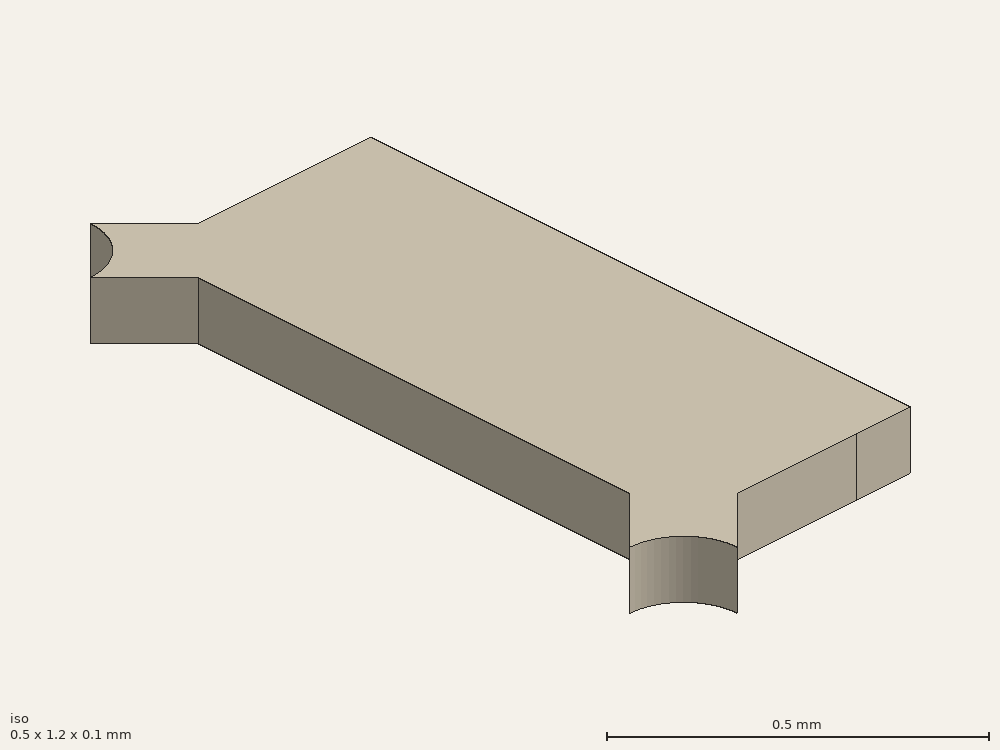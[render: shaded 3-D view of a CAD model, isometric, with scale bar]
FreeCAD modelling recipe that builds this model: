
FCSTD DOCUMENT  (FreeCAD 0.17R12607 (Git))
Label: FC-12M PAD 2bis
License: CreativeCommons Attribution-ShareAlike
LicenseURL: http://creativecommons.org/licenses/by-sa/4.0/
objects: Sketcher::SketchObject×1, PartDesign::Pad×1, PartDesign::Body×1
note: 4 computed .brp shape members not serialized (recipe doc carries the construction recipe); baked Part::Feature solids carry a one-line shape summary decoded from their .brp

FEATURE [Sketcher::SketchObject] Sketch
  MapMode = 5
  Support = -> [XY_Plane]
  sketch-geometry (19):
    g0: LineSegment StartX=-0.5 StartY=0.4 StartZ=0 EndX=-0.5 EndY=-0.4 EndZ=0
    g1: LineSegment [constr] StartX=-0.5 StartY=-0.4 StartZ=0 EndX=-0.6 EndY=-0.5 EndZ=0
    g2: LineSegment StartX=-0.6 StartY=-0.5 StartZ=0 EndX=-0.82 EndY=-0.5 EndZ=0
    g3: LineSegment StartX=-0.82 StartY=-0.5 StartZ=0 EndX=-0.92 EndY=-0.6 EndZ=0
    g4: LineSegment [constr] StartX=-0.92 StartY=-0.6 StartZ=0 EndX=-1.02 EndY=-0.5 EndZ=0
    g5: LineSegment StartX=-1.02 StartY=-0.5 StartZ=0 EndX=-0.92 EndY=-0.4 EndZ=0
    g6: LineSegment StartX=-0.92 StartY=-0.4 StartZ=0 EndX=-0.92 EndY=0.4 EndZ=0
    g7: LineSegment StartX=-0.92 StartY=0.4 StartZ=0 EndX=-1.02 EndY=0.5 EndZ=0
    g8: LineSegment [constr] StartX=-1.02 StartY=0.5 StartZ=0 EndX=-0.92 EndY=0.6 EndZ=0
    g9: LineSegment StartX=-0.92 StartY=0.6 StartZ=0 EndX=-0.82 EndY=0.5 EndZ=0
    g10: LineSegment StartX=-0.82 StartY=0.5 StartZ=0 EndX=-0.6 EndY=0.5 EndZ=0
    g11: LineSegment [constr] StartX=-0.6 StartY=0.5 StartZ=0 EndX=-0.5 EndY=0.4 EndZ=0
    g12: ArcOfCircle CenterX=-1.02 CenterY=0.6 CenterZ=0 NormalX=0 NormalY=0 NormalZ=1 AngleXU=0 Radius=0.1 StartAngle=4.71239 EndAngle=6.28319
    g13: LineSegment [constr] StartX=-1.02 StartY=0.5 StartZ=0 EndX=-0.82 EndY=0.5 EndZ=0
    g14: ArcOfCircle CenterX=-1.02 CenterY=-0.6 CenterZ=0 NormalX=0 NormalY=0 NormalZ=1 AngleXU=0 Radius=0.1 StartAngle=6.28319 EndAngle=7.85398
    g15: LineSegment StartX=-0.6 StartY=-0.5 StartZ=0 EndX=-0.5 EndY=-0.5 EndZ=0
    g16: LineSegment StartX=-0.5 StartY=-0.5 StartZ=0 EndX=-0.5 EndY=-0.4 EndZ=0
    g17: LineSegment StartX=-0.6 StartY=0.5 StartZ=0 EndX=-0.5 EndY=0.5 EndZ=0
    g18: LineSegment StartX=-0.5 StartY=0.5 StartZ=0 EndX=-0.5 EndY=0.4 EndZ=0
  constraints (52):
    c: Vertical(g0)
    c: Coincident(g0,g1)
    c: Coincident(g1,g2)
    c: Horizontal(g2)
    c: Coincident(g2,g3)
    c: Coincident(g3,g4)
    c: Coincident(g4,g5)
    c: Coincident(g5,g6)
    c: Vertical(g6)
    c: Coincident(g6,g7)
    c: Coincident(g7,g8)
    c: Coincident(g8,g9)
    c: Coincident(g9,g10)
    c: Horizontal(g10)
    c: Coincident(g10,g11)
    c: Coincident(g11,g0)
    c: Perpendicular(g7,g8)
    c: Perpendicular(g9,g8)
    c: Symmetric(g0,g0,g-1)
    c: Symmetric(g1,g10,g-1)
    c: Symmetric(g9,g2,g-1)
    c: Symmetric(g8,g3,g-1)
    c: Symmetric(g7,g4,g-1)
    c: Symmetric(g6,g5,g-1)
    c: DistanceX(g-2,g0) = -0.5
    c: Angle(g11,g0) = 2.35619
    c: DistanceX(g10,g10) = 0.22
    c: DistanceY(g0,g0) = 0.8
    c: Equal(g0,g6)
    c: Distance(g5,g0) = 0.42
    c: Angle(g7,g6) = 2.35619
    c: Equal(g8,g9)
    c: Distance(g4,g0) = 0.52
    c: Coincident(g12,g7)
    c: Coincident(g12,g8)
    c: Coincident(g13,g7)
    c: Coincident(g13,g9)
    c: Horizontal(g13)
    c: Tangent(g13,g12)
    c: Coincident(g14,g3)
    c: Coincident(g14,g4)
    c: Symmetric(g12,g14,g-1)
    c: Coincident(g1,g15)
    c: Horizontal(g15)
    c: Coincident(g15,g16)
    c: Coincident(g16,g0)
    c: Vertical(g16)
    c: Coincident(g10,g17)
    c: Horizontal(g17)
    c: Coincident(g17,g18)
    c: Coincident(g18,g0)
    c: Vertical(g18)
FEATURE [PartDesign::Pad] Pad
  Length = 0.1
  Length2 = 100
  Profile = -> Sketch
  Type = 0
FEATURE [PartDesign::Body] Body
  Group = -> [Sketch,Pad]
  Origin = -> Origin
  Tip = -> Pad
